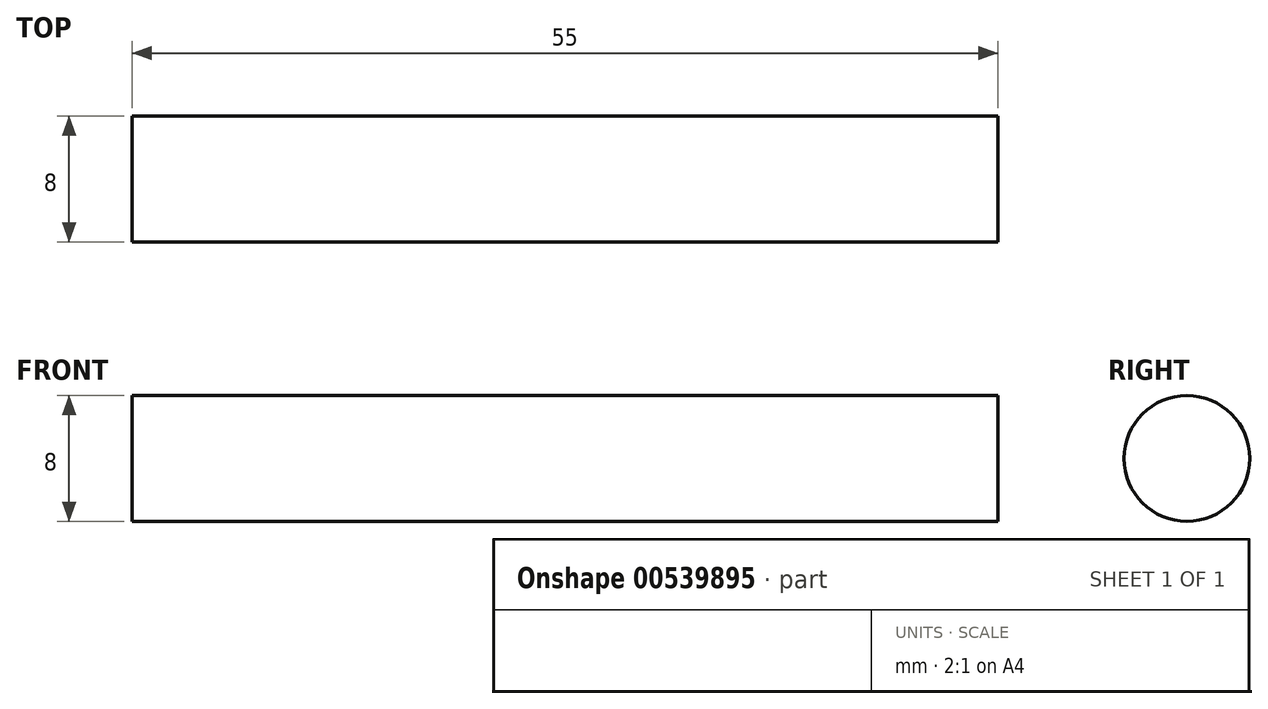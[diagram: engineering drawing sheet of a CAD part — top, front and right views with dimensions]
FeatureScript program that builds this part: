
annotation { "Feature Type Name" : "Feature", "Feature Type Description" : "" }
export const myFeature = defineFeature(function(context is Context, id is Id, definition is map)
    precondition{}
    {
        {
            var Q0;
            Q0=qCreatedBy(makeId("Right.planeOp"),FACE);
            var sketch = newSketch(context, id + "F0", { "sketchPlane" : qUnion([Q0])});
            skCircle(sketch, "E0", {"center": v(0, 0) * mm, "radius": 4 * mm});
            skSolve(sketch);
        }
        {
            var Q0;
            Q0=makeQuery(id+"F0.imprint","IMPRINT",FACE,{"disambiguationData":[TD([[makeQuery(id+"F0.imprint","IMPRINT",EDGE,{"derivedFrom":sQuery(id+"F0.wireOp",EDGE,"E0")}),1.0]])]});
            extrude(context, id + "F1", {"entities" : qUnion([Q0]), "endBound" : BoundingType.SYMMETRIC, "depth" : 55 * mm, "offsetDistance" : 25 * mm});
        }
    });
